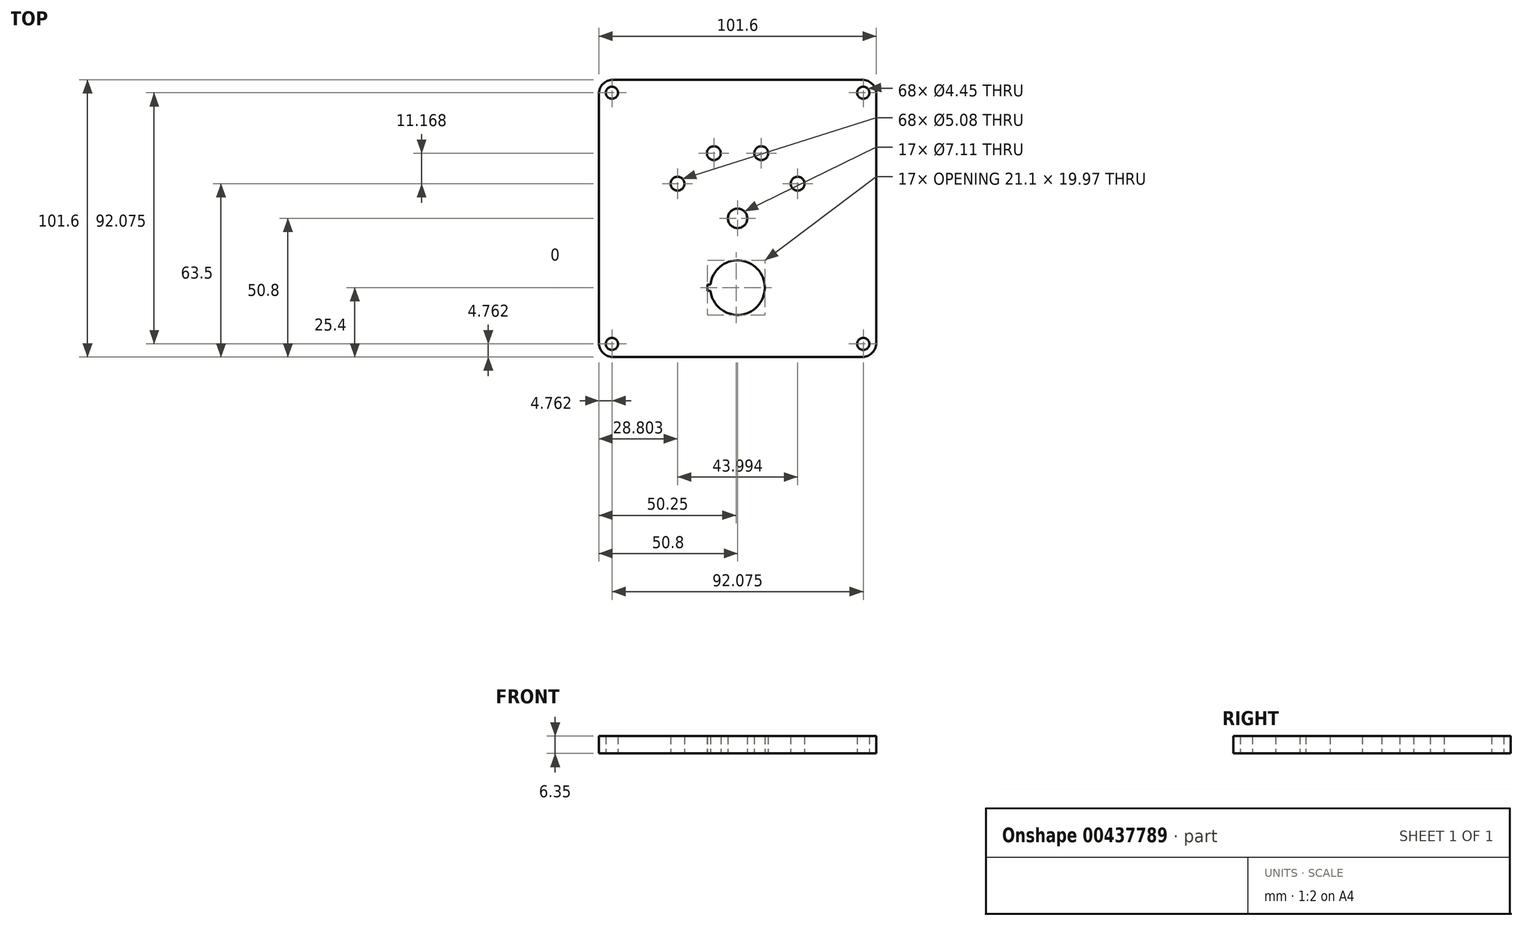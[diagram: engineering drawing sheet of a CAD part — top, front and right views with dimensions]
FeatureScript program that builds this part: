
annotation { "Feature Type Name" : "Feature", "Feature Type Description" : "" }
export const myFeature = defineFeature(function(context is Context, id is Id, definition is map)
    precondition{}
    {
        {
            var Q0;
            Q0=qCreatedBy(makeId("Top.planeOp"),FACE);
            var sketch = newSketch(context, id + "F0", { "sketchPlane" : qUnion([Q0])});
            skLineSegment(sketch, "E0.bottom", {"start": v(-45.72, 50.8) * mm, "end": v(45.72, 50.8) * mm});
            skLineSegment(sketch, "E0.top", {"start": v(-45.72, -50.8) * mm, "end": v(45.72, -50.8) * mm});
            skLineSegment(sketch, "E0.left", {"start": v(-50.8, 45.72) * mm, "end": v(-50.8, -45.72) * mm});
            skLineSegment(sketch, "E0.right", {"start": v(50.8, 45.72) * mm, "end": v(50.8, -45.72) * mm});
            skCircle(sketch, "E1", {"center": v(-46.04, 46.04) * mm, "radius": 2.22 * mm});
            skCircle(sketch, "E2.0.1.0", {"center": v(-46.04, -46.04) * mm, "radius": 2.22 * mm});
            skCircle(sketch, "E2.1.0.0", {"center": v(46.04, 46.04) * mm, "radius": 2.22 * mm});
            skCircle(sketch, "E2.1.1.0", {"center": v(46.04, -46.04) * mm, "radius": 2.22 * mm});
            skLineSegment(sketch, "E2.direction1", {"start": v(-46.04, 46.04) * mm, "end": v(46.04, 46.04) * mm, "construction": true});
            skLineSegment(sketch, "E2.direction2", {"start": v(-46.04, 46.04) * mm, "end": v(-46.04, -46.04) * mm, "construction": true});
            skArc(sketch, "E3", {"start": v(-9.94, -26.5) * mm, "mid": v(10, -25.4) * mm, "end": v(-9.94, -24.3) * mm});
            skLineSegment(sketch, "E4", {"start": v(0, -25.4) * mm, "end": v(-23.51, -25.4) * mm, "construction": true});
            skLineSegment(sketch, "E5", {"start": v(-11.1, -25.4) * mm, "end": v(-11.1, -24.3) * mm});
            skLineSegment(sketch, "E6", {"start": v(-11.1, -24.3) * mm, "end": v(-9.94, -24.3) * mm});
            skLineSegment(sketch, "E7.MirrorCS", {"start": v(-11.1, -25.4) * mm, "end": v(-11.1, -26.5) * mm});
            skLineSegment(sketch, "E8.MirrorCS", {"start": v(-11.1, -26.5) * mm, "end": v(-9.94, -26.5) * mm});
            skPoint(sketch, "E9", {"position": v(-50.8, 0) * mm});
            skPoint(sketch, "E10", {"position": v(0, 50.8) * mm});
            skCircle(sketch, "E11", {"center": v(-22, 12.7) * mm, "radius": 2.54 * mm});
            skPoint(sketch, "E12.visualSharp", {"position": v(-50.8, 50.8) * mm});
            skArc(sketch, "E12.filletArc", {"start": v(-45.72, 50.8) * mm, "mid": v(-49.31, 49.31) * mm, "end": v(-50.8, 45.72) * mm});
            skPoint(sketch, "E13.visualSharp", {"position": v(50.8, 50.8) * mm});
            skArc(sketch, "E13.filletArc", {"start": v(50.8, 45.72) * mm, "mid": v(49.31, 49.31) * mm, "end": v(45.72, 50.8) * mm});
            skPoint(sketch, "E14.visualSharp", {"position": v(50.8, -50.8) * mm});
            skArc(sketch, "E14.filletArc", {"start": v(45.72, -50.8) * mm, "mid": v(49.31, -49.31) * mm, "end": v(50.8, -45.72) * mm});
            skPoint(sketch, "E15.visualSharp", {"position": v(-50.8, -50.8) * mm});
            skArc(sketch, "E15.filletArc", {"start": v(-50.8, -45.72) * mm, "mid": v(-49.31, -49.31) * mm, "end": v(-45.72, -50.8) * mm});
            skCircle(sketch, "E16", {"center": v(0, 0) * mm, "radius": 3.56 * mm});
            skCircle(sketch, "E17", {"center": v(0, 0) * mm, "radius": 25.4 * mm, "construction": true});
            skCircle(sketch, "E18.1.0", {"center": v(-8.69, 23.87) * mm, "radius": 2.54 * mm});
            skCircle(sketch, "E18.2.0", {"center": v(8.69, 23.87) * mm, "radius": 2.54 * mm});
            skCircle(sketch, "E18.3.0", {"center": v(22, 12.7) * mm, "radius": 2.54 * mm});
            skLineSegment(sketch, "E18.anchor1", {"start": v(0, 0) * mm, "end": v(-22, 12.7) * mm, "construction": true});
            skLineSegment(sketch, "E18.anchor2", {"start": v(0, 0) * mm, "end": v(22, 12.7) * mm, "construction": true});
            skSolve(sketch);
        }
        {
            var Q0;
            Q0=makeQuery(id+"F0.imprint","IMPRINT",FACE,{"disambiguationData":[TD([[makeQuery(id+"F0.imprint","IMPRINT",EDGE,{"derivedFrom":sQuery(id+"F0.wireOp",EDGE,"E0.bottom")}),-1.0]])]});
            extrude(context, id + "F1", {"entities" : qUnion([Q0]), "depth" : 6.35 * mm, "offsetDistance" : 25.4 * mm});
        }
    });
